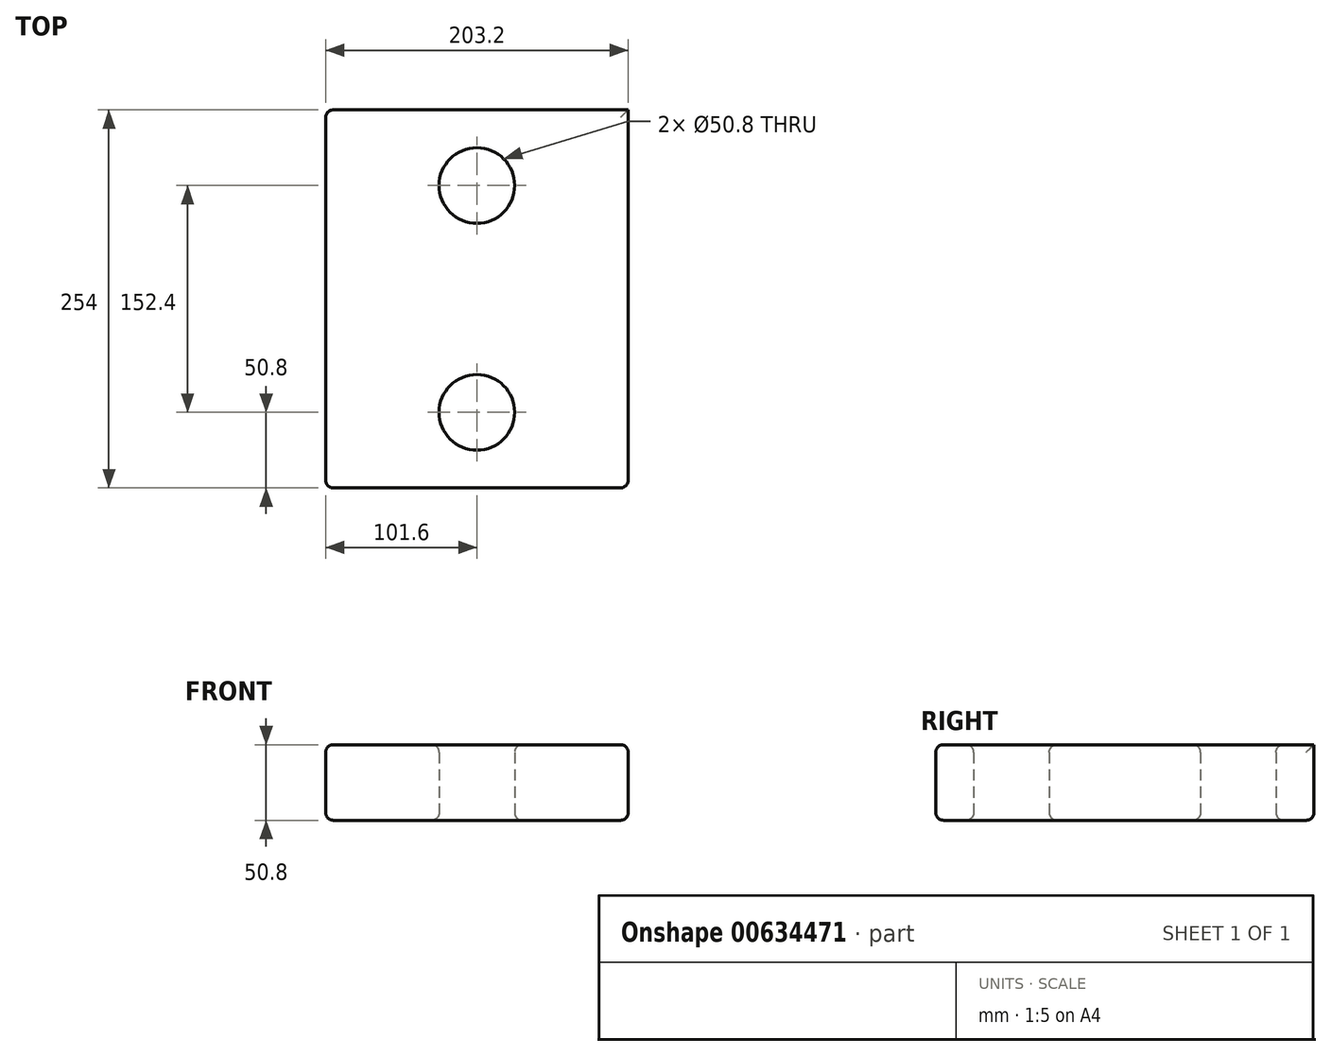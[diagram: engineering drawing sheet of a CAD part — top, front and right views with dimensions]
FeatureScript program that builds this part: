
annotation { "Feature Type Name" : "Feature", "Feature Type Description" : "" }
export const myFeature = defineFeature(function(context is Context, id is Id, definition is map)
    precondition{}
    {
        {
            var Q0;
            Q0=qCreatedBy(makeId("Top.planeOp"),FACE);
            var sketch = newSketch(context, id + "F0", { "sketchPlane" : qUnion([Q0])});
            skLineSegment(sketch, "E0.bottom", {"start": v(0, 0) * mm, "end": v(203.2, 0) * mm});
            skLineSegment(sketch, "E0.top", {"start": v(0, 254) * mm, "end": v(203.2, 254) * mm});
            skLineSegment(sketch, "E0.left", {"start": v(0, 0) * mm, "end": v(0, 254) * mm});
            skLineSegment(sketch, "E0.right", {"start": v(203.2, 0) * mm, "end": v(203.2, 254) * mm});
            skLineSegment(sketch, "E1", {"start": v(0, 127) * mm, "end": v(203.2, 127) * mm, "construction": true});
            skCircle(sketch, "E2", {"center": v(101.6, 203.2) * mm, "radius": 25.4 * mm});
            skPoint(sketch, "E2.centerSnap0", {"position": v(101.6, 254) * mm});
            skCircle(sketch, "E3.MirrorC", {"center": v(101.6, 50.8) * mm, "radius": 25.4 * mm});
            skSolve(sketch);
        }
        {
            var Q0;
            Q0=makeQuery(id+"F0.imprint","IMPRINT",FACE,{"disambiguationData":[TD([[makeQuery(id+"F0.imprint","IMPRINT",EDGE,{"derivedFrom":sQuery(id+"F0.wireOp",EDGE,"E0.bottom")}),1.0]])]});
            extrude(context, id + "F1", {"entities" : qUnion([Q0]), "depth" : 50.8 * mm, "offsetDistance" : 25.4 * mm});
        }
        {
            var Q0;
            Q0=makeQuery(id+"F1.opExtrude","CAP_EDGE",EDGE,{"disambiguationData":[OSD([sQuery(id+"F0.wireOp",EDGE,"E0.top")])],"isStart":true});
            var Q1;
            Q1=makeQuery(id+"F1.opExtrude","CAP_EDGE",EDGE,{"disambiguationData":[OSD([sQuery(id+"F0.wireOp",EDGE,"E2")])],"isStart":true});
            var Q2;
            Q2=makeQuery(id+"F1.opExtrude","CAP_EDGE",EDGE,{"disambiguationData":[OSD([sQuery(id+"F0.wireOp",EDGE,"E0.left")])],"isStart":true});
            var Q3;
            Q3=makeQuery(id+"F1.opExtrude","CAP_EDGE",EDGE,{"disambiguationData":[OSD([sQuery(id+"F0.wireOp",EDGE,"E0.left")])],"isStart":false});
            var Q4;
            Q4=makeQuery(id+"F1.opExtrude","SWEPT_EDGE",EDGE,{"disambiguationData":[OSD([sQuery(id+"F0.wireOp",EDGE,"E0.top"),sQuery(id+"F0.wireOp",EDGE,"E0.left")])]});
            var Q5;
            Q5=makeQuery(id+"F1.opExtrude","CAP_EDGE",EDGE,{"disambiguationData":[OSD([sQuery(id+"F0.wireOp",EDGE,"E3.MirrorC")])],"isStart":true});
            var Q6;
            Q6=makeQuery(id+"F1.opExtrude","CAP_EDGE",EDGE,{"disambiguationData":[OSD([sQuery(id+"F0.wireOp",EDGE,"E0.right")])],"isStart":true});
            var Q7;
            Q7=makeQuery(id+"F1.opExtrude","CAP_FACE",FACE,{"disambiguationData":[OSD([sQuery(id+"F0.wireOp",EDGE,"E0.bottom"),sQuery(id+"F0.wireOp",EDGE,"E0.top"),sQuery(id+"F0.wireOp",EDGE,"E0.left"),sQuery(id+"F0.wireOp",EDGE,"E0.right"),sQuery(id+"F0.wireOp",EDGE,"E2"),sQuery(id+"F0.wireOp",EDGE,"E3.MirrorC")])],"isStart":true});
            var Q8;
            Q8=makeQuery(id+"F1.opExtrude","SWEPT_EDGE",EDGE,{"disambiguationData":[OSD([sQuery(id+"F0.wireOp",EDGE,"E0.bottom"),sQuery(id+"F0.wireOp",EDGE,"E0.left")])]});
            var Q9;
            Q9=makeQuery(id+"F1.opExtrude","CAP_EDGE",EDGE,{"disambiguationData":[OSD([sQuery(id+"F0.wireOp",EDGE,"E2")])],"isStart":false});
            var Q10;
            Q10=makeQuery(id+"F1.opExtrude","CAP_EDGE",EDGE,{"disambiguationData":[OSD([sQuery(id+"F0.wireOp",EDGE,"E3.MirrorC")])],"isStart":false});
            var Q11;
            Q11=makeQuery(id+"F1.opExtrude","SWEPT_EDGE",EDGE,{"disambiguationData":[OSD([sQuery(id+"F0.wireOp",EDGE,"E0.bottom"),sQuery(id+"F0.wireOp",EDGE,"E0.right")])]});
            var Q12;
            Q12=makeQuery(id+"F1.opExtrude","CAP_EDGE",EDGE,{"disambiguationData":[OSD([sQuery(id+"F0.wireOp",EDGE,"E0.bottom")])],"isStart":false});
            var Q13;
            Q13=makeQuery(id+"F1.opExtrude","CAP_EDGE",EDGE,{"disambiguationData":[OSD([sQuery(id+"F0.wireOp",EDGE,"E0.right")])],"isStart":false});
            fillet(context, id + "F2", {"entities" : qUnion([Q0, Q1, Q2, Q3, Q4, Q5, Q6, Q7, Q8, Q9, Q10, Q11, Q12, Q13]), "radius" : 5.08 * mm, "tangentPropagation" : true, "allowEdgeOverflow" : false});
        }
    });
